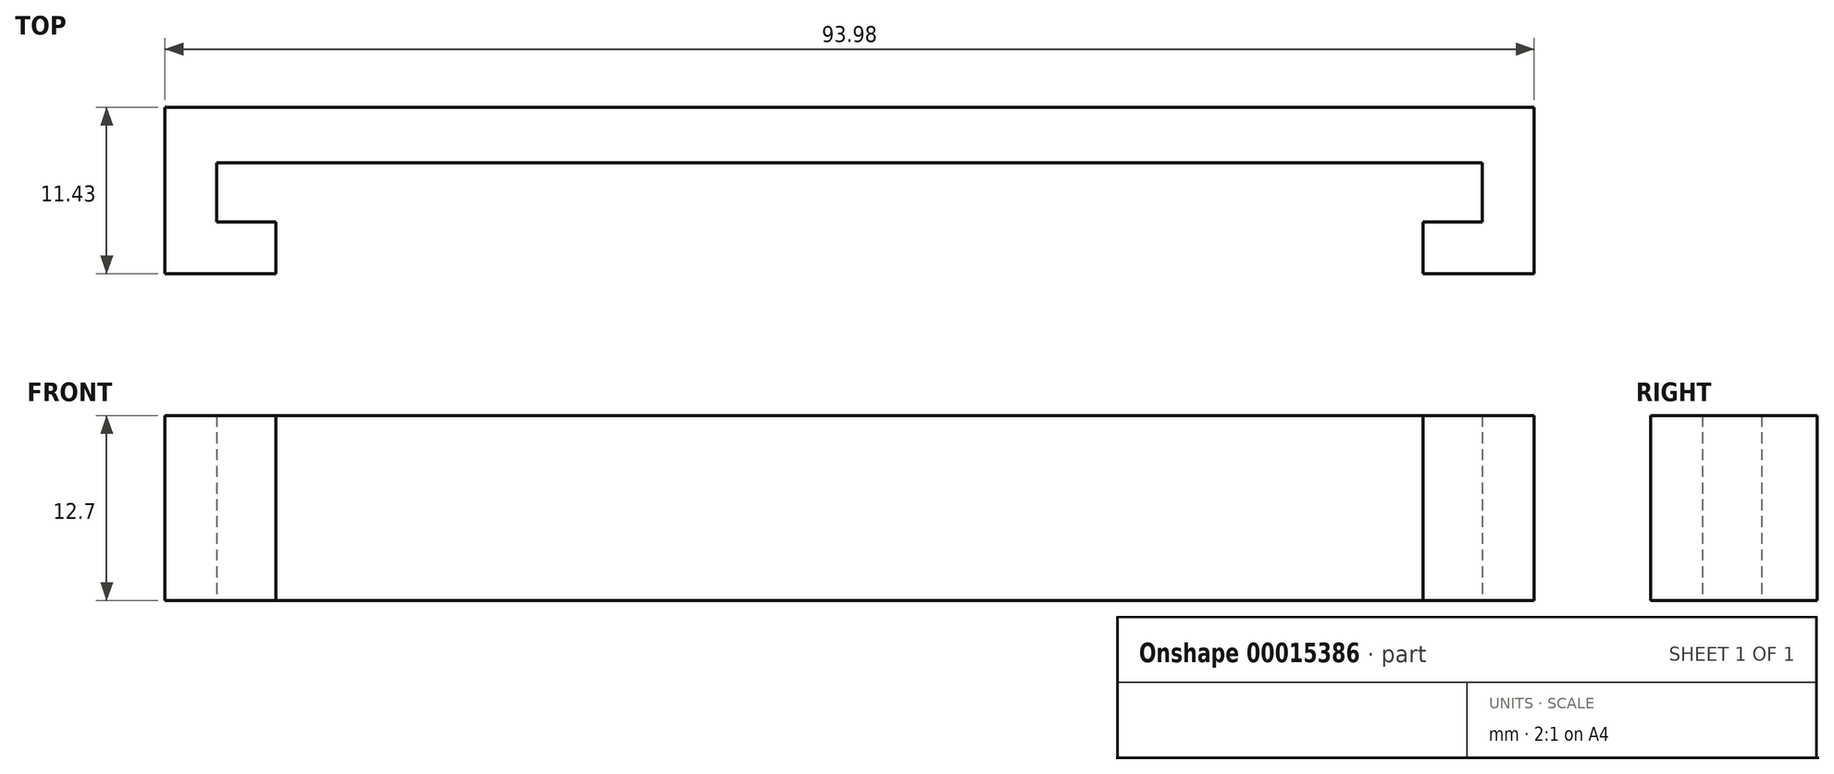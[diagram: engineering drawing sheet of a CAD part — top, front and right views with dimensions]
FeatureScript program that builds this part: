
annotation { "Feature Type Name" : "Feature", "Feature Type Description" : "" }
export const myFeature = defineFeature(function(context is Context, id is Id, definition is map)
    precondition{}
    {
        {
            var Q0;
            Q0=qCreatedBy(makeId("Top.planeOp"),FACE);
            var sketch = newSketch(context, id + "F0", { "sketchPlane" : qUnion([Q0])});
            skLineSegment(sketch, "E0", {"start": v(-17.32, -7.84) * mm, "end": v(-24.94, -7.84) * mm});
            skLineSegment(sketch, "E1", {"start": v(-24.94, -7.84) * mm, "end": v(-24.94, 3.59) * mm});
            skLineSegment(sketch, "E2", {"start": v(-24.94, 3.59) * mm, "end": v(69.04, 3.59) * mm});
            skLineSegment(sketch, "E3", {"start": v(69.04, 3.59) * mm, "end": v(69.04, -7.84) * mm});
            skLineSegment(sketch, "E4", {"start": v(69.04, -7.84) * mm, "end": v(61.42, -7.84) * mm});
            skLineSegment(sketch, "E5", {"start": v(61.42, -7.84) * mm, "end": v(61.42, -4.28) * mm});
            skLineSegment(sketch, "E6", {"start": v(61.42, -4.28) * mm, "end": v(65.48, -4.28) * mm});
            skLineSegment(sketch, "E7", {"start": v(65.48, -4.28) * mm, "end": v(65.48, -0.22) * mm});
            skLineSegment(sketch, "E8", {"start": v(65.48, -0.22) * mm, "end": v(-21.39, -0.22) * mm});
            skLineSegment(sketch, "E9", {"start": v(-21.39, -0.22) * mm, "end": v(-21.39, -4.28) * mm});
            skLineSegment(sketch, "E10", {"start": v(-21.39, -4.28) * mm, "end": v(-17.32, -4.28) * mm});
            skLineSegment(sketch, "E11", {"start": v(-17.32, -4.28) * mm, "end": v(-17.32, -7.84) * mm});
            skSolve(sketch);
        }
        {
            var Q0;
            Q0=qSketchRegion(id+"F0",true);
            extrude(context, id + "F1", {"entities" : qUnion([Q0]), "depth" : 12.7 * mm});
        }
    });
